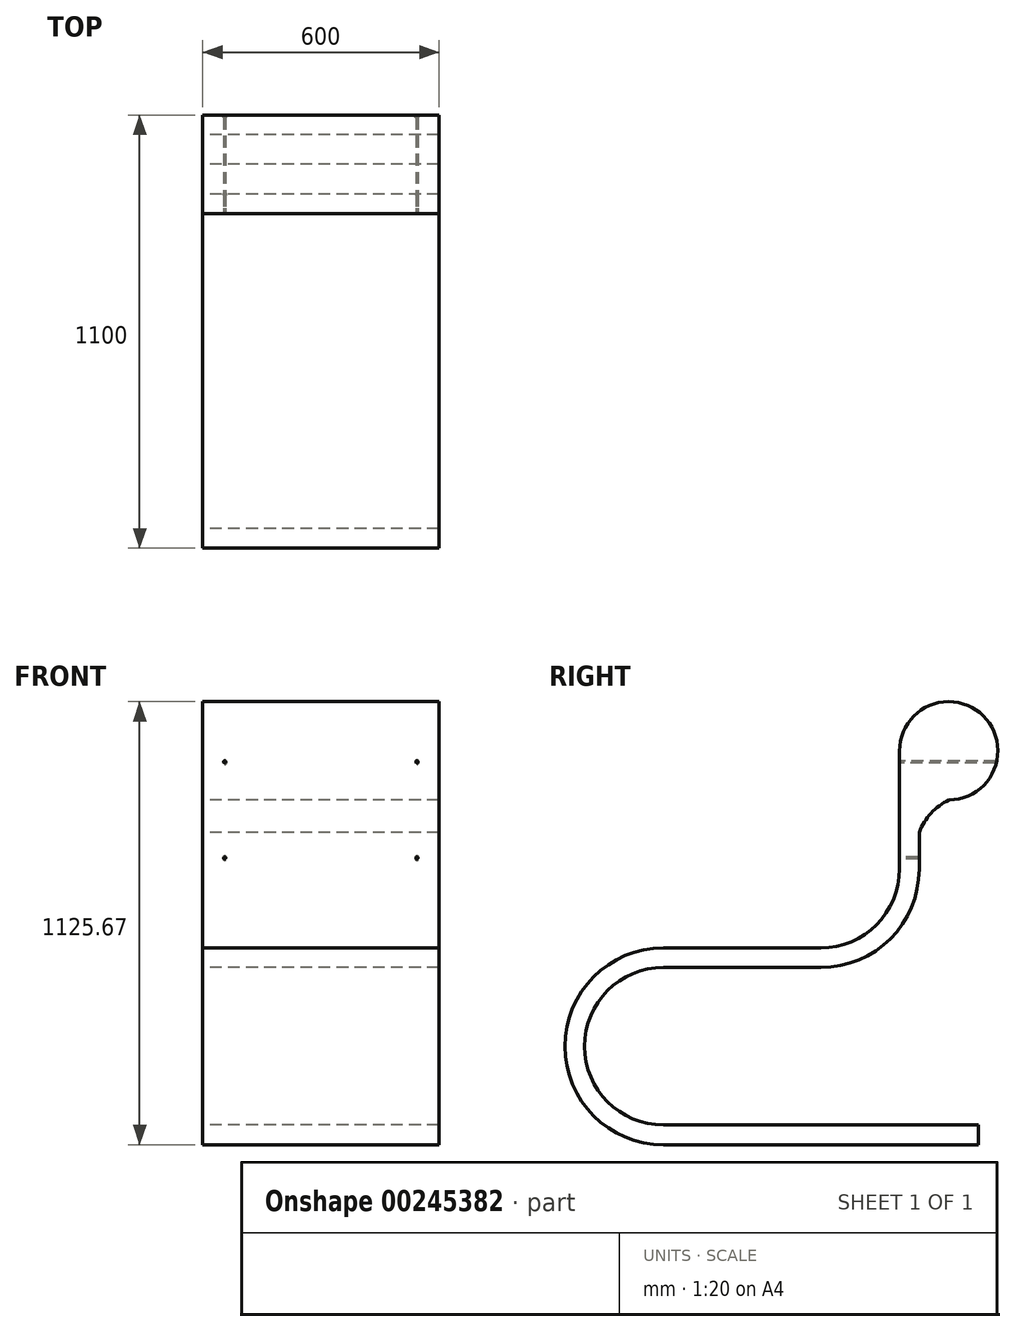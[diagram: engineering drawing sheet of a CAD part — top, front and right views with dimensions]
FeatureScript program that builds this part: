
annotation { "Feature Type Name" : "Feature", "Feature Type Description" : "" }
export const myFeature = defineFeature(function(context is Context, id is Id, definition is map)
    precondition{}
    {
        {
            var Q0;
            Q0=qCreatedBy(makeId("Right.planeOp"),FACE);
            var sketch = newSketch(context, id + "F0", { "sketchPlane" : qUnion([Q0])});
            skLineSegment(sketch, "E0", {"start": v(0, 0) * mm, "end": v(200, 0) * mm});
            skLineSegment(sketch, "E1", {"start": v(0, 0) * mm, "end": v(-200, 0) * mm});
            skLineSegment(sketch, "E2", {"start": v(200, 0) * mm, "end": v(200, 200) * mm});
            skArc(sketch, "E3", {"start": v(200, 0) * mm, "mid": v(341.42, 58.58) * mm, "end": v(400, 200) * mm});
            skLineSegment(sketch, "E4", {"start": v(-200, 0) * mm, "end": v(-200, -500) * mm});
            skArc(sketch, "E5", {"start": v(-200, 0) * mm, "mid": v(-450, -250) * mm, "end": v(-200, -500) * mm});
            skPoint(sketch, "E6", {"position": v(-200, -50) * mm});
            skPoint(sketch, "E7", {"position": v(-200, -450) * mm});
            skArc(sketch, "E8", {"start": v(-200, -50) * mm, "mid": v(-400, -250) * mm, "end": v(-200, -450) * mm});
            skLineSegment(sketch, "E9", {"start": v(-200, -50) * mm, "end": v(200, -50) * mm});
            skArc(sketch, "E10", {"start": v(200, -50) * mm, "mid": v(376.78, 23.22) * mm, "end": v(450, 200) * mm});
            skLineSegment(sketch, "E11.bottom", {"start": v(-200, -450) * mm, "end": v(600, -450) * mm});
            skLineSegment(sketch, "E11.top", {"start": v(-200, -500) * mm, "end": v(600, -500) * mm});
            skLineSegment(sketch, "E11.left", {"start": v(-200, -450) * mm, "end": v(-200, -500) * mm});
            skLineSegment(sketch, "E11.right", {"start": v(600, -450) * mm, "end": v(600, -500) * mm});
            skLineSegment(sketch, "E12.bottom", {"start": v(400, 200) * mm, "end": v(450, 200) * mm});
            skLineSegment(sketch, "E12.top", {"start": v(400, 500.67) * mm, "end": v(450, 500.67) * mm});
            skLineSegment(sketch, "E12.left", {"start": v(400, 200) * mm, "end": v(400, 500.67) * mm});
            skLineSegment(sketch, "E12.right", {"start": v(450, 200) * mm, "end": v(450, 500.67) * mm});
            skArc(sketch, "E13", {"start": v(400, 500.67) * mm, "mid": v(636.8, 556.57) * mm, "end": v(450, 400.67) * mm});
            skArc(sketch, "E14", {"start": v(526.03, 375.68) * mm, "mid": v(480.12, 342.1) * mm, "end": v(450, 293.85) * mm});
            skSolve(sketch);
        }
        {
            var Q0;
            {var subQ0=sQuery(id+"F0.wireOp",EDGE,"E12.top");Q0=makeQuery(id+"F0.imprint","IMPRINT",FACE,{"disambiguationData":[TD([[makeQuery(id+"F0.imprint","IMPRINT",EDGE,{"derivedFrom":subQ0}),1.0]])]});}
            var Q1;
            {var subQ3=sQuery(id+"F0.wireOp",EDGE,"E14");Q1=makeQuery(id+"F0.imprint","IMPRINT",FACE,{"disambiguationData":[TD([[makeQuery(id+"F0.imprint","IMPRINT",EDGE,{"derivedFrom":subQ3}),-1.0]])]});}
            var Q2;
            {var subQ1=sQuery(id+"F0.wireOp",EDGE,"E12.bottom");Q2=makeQuery(id+"F0.imprint","IMPRINT",FACE,{"disambiguationData":[TD([[makeQuery(id+"F0.imprint","IMPRINT",EDGE,{"derivedFrom":subQ1}),1.0]])]});}
            var Q3;
            Q3=makeQuery(id+"F0.imprint","IMPRINT",FACE,{"disambiguationData":[TD([[makeQuery(id+"F0.imprint","IMPRINT",EDGE,{"derivedFrom":sQuery(id+"F0.wireOp",EDGE,"E0")}),-1.0]])]});
            var Q4;
            {var subQ0=sQuery(id+"F0.wireOp",EDGE,"E5");Q4=makeQuery(id+"F0.imprint","IMPRINT",FACE,{"disambiguationData":[TD([[makeQuery(id+"F0.imprint","IMPRINT",EDGE,{"derivedFrom":subQ0}),1.0]])]});}
            var Q5;
            Q5=makeQuery(id+"F0.imprint","IMPRINT",FACE,{"disambiguationData":[TD([[makeQuery(id+"F0.imprint","IMPRINT",EDGE,{"derivedFrom":sQuery(id+"F0.wireOp",EDGE,"E11.bottom")}),-1.0]])]});
            extrude(context, id + "F1", {"entities" : qUnion([Q0, Q1, Q2, Q3, Q4, Q5]), "depth" : 600 * mm});
        }
        {
            var Q0;
            Q0=makeQuery(id+"F1.opExtrude","SWEPT_FACE",FACE,{"disambiguationData":[OSD([sQuery(id+"F0.wireOp",EDGE,"E12.left")])]});
            var sketch = newSketch(context, id + "F2", { "sketchPlane" : qUnion([Q0])});
            skLineSegment(sketch, "E15", {"start": v(0, 500.67) * mm, "end": v(600, 200) * mm});
            skLineSegment(sketch, "E16", {"start": v(600, 500.67) * mm, "end": v(0, 200) * mm});
            skLineSegment(sketch, "E17", {"start": v(55.87, 472.67) * mm, "end": v(55.87, 228) * mm});
            skLineSegment(sketch, "E18", {"start": v(55.87, 228) * mm, "end": v(544.13, 228) * mm});
            skLineSegment(sketch, "E19", {"start": v(544.13, 228) * mm, "end": v(544.13, 472.67) * mm});
            skLineSegment(sketch, "E20", {"start": v(544.13, 472.67) * mm, "end": v(55.87, 472.67) * mm});
            skCircle(sketch, "E21", {"center": v(55.87, 228) * mm, "radius": 2.5 * mm});
            skCircle(sketch, "E22", {"center": v(55.87, 472.67) * mm, "radius": 2.5 * mm});
            skCircle(sketch, "E23", {"center": v(544.13, 472.67) * mm, "radius": 2.5 * mm});
            skCircle(sketch, "E24", {"center": v(544.13, 228) * mm, "radius": 2.5 * mm});
            skSolve(sketch);
        }
        {
            var Q0;
            {var subQ1=sQuery(id+"F2.wireOp",EDGE,"E15");var subQ3=sQuery(id+"F2.wireOp",EDGE,"E22");var subQ4=makeQuery(id+"F2.imprint","INTERSECT",VERTEX,{"disambiguationData":[OD(0.0)],"derivedFrom":[subQ1,subQ3]});Q0=makeQuery(id+"F2.imprint","IMPRINT",FACE,{"disambiguationData":[TD([[makeQuery(id+"F2.imprint","IMPRINT",EDGE,{"disambiguationData":[TD([[subQ4,-1.0]])],"derivedFrom":subQ3}),1.0]])]});}
            var Q1;
            {var subQ1=sQuery(id+"F2.wireOp",EDGE,"E15");var subQ3=sQuery(id+"F2.wireOp",EDGE,"E22");var subQ4=makeQuery(id+"F2.imprint","INTERSECT",VERTEX,{"disambiguationData":[OD(0.0)],"derivedFrom":[subQ1,subQ3]});Q1=makeQuery(id+"F2.imprint","IMPRINT",FACE,{"disambiguationData":[TD([[makeQuery(id+"F2.imprint","IMPRINT",EDGE,{"disambiguationData":[TD([[subQ4,1.0]])],"derivedFrom":subQ3}),1.0]])]});}
            var Q2;
            {var subQ1=sQuery(id+"F2.wireOp",EDGE,"E15");var subQ3=sQuery(id+"F2.wireOp",EDGE,"E22");var subQ4=makeQuery(id+"F2.imprint","INTERSECT",VERTEX,{"disambiguationData":[OD(1.0)],"derivedFrom":[subQ1,subQ3]});Q2=makeQuery(id+"F2.imprint","IMPRINT",FACE,{"disambiguationData":[TD([[makeQuery(id+"F2.imprint","IMPRINT",EDGE,{"disambiguationData":[TD([[subQ4,1.0]])],"derivedFrom":subQ3}),1.0]])]});}
            var Q3;
            {var subQ1=sQuery(id+"F2.wireOp",EDGE,"E15");var subQ3=sQuery(id+"F2.wireOp",EDGE,"E22");var subQ4=makeQuery(id+"F2.imprint","INTERSECT",VERTEX,{"disambiguationData":[OD(1.0)],"derivedFrom":[subQ1,subQ3]});Q3=makeQuery(id+"F2.imprint","IMPRINT",FACE,{"disambiguationData":[TD([[makeQuery(id+"F2.imprint","IMPRINT",EDGE,{"disambiguationData":[TD([[subQ4,-1.0]])],"derivedFrom":subQ3}),1.0]])]});}
            var Q4;
            {var subQ1=sQuery(id+"F2.wireOp",EDGE,"E16");var subQ3=sQuery(id+"F2.wireOp",EDGE,"E21");var subQ4=makeQuery(id+"F2.imprint","INTERSECT",VERTEX,{"disambiguationData":[OD(0.0)],"derivedFrom":[subQ1,subQ3]});Q4=makeQuery(id+"F2.imprint","IMPRINT",FACE,{"disambiguationData":[TD([[makeQuery(id+"F2.imprint","IMPRINT",EDGE,{"disambiguationData":[TD([[subQ4,1.0]])],"derivedFrom":subQ3}),1.0]])]});}
            var Q5;
            {var subQ1=sQuery(id+"F2.wireOp",EDGE,"E16");var subQ3=sQuery(id+"F2.wireOp",EDGE,"E21");var subQ4=makeQuery(id+"F2.imprint","INTERSECT",VERTEX,{"disambiguationData":[OD(0.0)],"derivedFrom":[subQ1,subQ3]});Q5=makeQuery(id+"F2.imprint","IMPRINT",FACE,{"disambiguationData":[TD([[makeQuery(id+"F2.imprint","IMPRINT",EDGE,{"disambiguationData":[TD([[subQ4,-1.0]])],"derivedFrom":subQ3}),1.0]])]});}
            var Q6;
            {var subQ1=sQuery(id+"F2.wireOp",EDGE,"E16");var subQ3=sQuery(id+"F2.wireOp",EDGE,"E21");var subQ4=makeQuery(id+"F2.imprint","INTERSECT",VERTEX,{"disambiguationData":[OD(1.0)],"derivedFrom":[subQ1,subQ3]});Q6=makeQuery(id+"F2.imprint","IMPRINT",FACE,{"disambiguationData":[TD([[makeQuery(id+"F2.imprint","IMPRINT",EDGE,{"disambiguationData":[TD([[subQ4,1.0]])],"derivedFrom":subQ3}),1.0]])]});}
            var Q7;
            {var subQ1=sQuery(id+"F2.wireOp",EDGE,"E16");var subQ3=sQuery(id+"F2.wireOp",EDGE,"E21");var subQ4=makeQuery(id+"F2.imprint","INTERSECT",VERTEX,{"disambiguationData":[OD(1.0)],"derivedFrom":[subQ1,subQ3]});Q7=makeQuery(id+"F2.imprint","IMPRINT",FACE,{"disambiguationData":[TD([[makeQuery(id+"F2.imprint","IMPRINT",EDGE,{"disambiguationData":[TD([[subQ4,-1.0]])],"derivedFrom":subQ3}),1.0]])]});}
            var Q8;
            {var subQ1=sQuery(id+"F2.wireOp",EDGE,"E15");var subQ3=sQuery(id+"F2.wireOp",EDGE,"E24");var subQ4=makeQuery(id+"F2.imprint","INTERSECT",VERTEX,{"disambiguationData":[OD(0.0)],"derivedFrom":[subQ1,subQ3]});Q8=makeQuery(id+"F2.imprint","IMPRINT",FACE,{"disambiguationData":[TD([[makeQuery(id+"F2.imprint","IMPRINT",EDGE,{"disambiguationData":[TD([[subQ4,1.0]])],"derivedFrom":subQ3}),1.0]])]});}
            var Q9;
            {var subQ1=sQuery(id+"F2.wireOp",EDGE,"E15");var subQ3=sQuery(id+"F2.wireOp",EDGE,"E24");var subQ4=makeQuery(id+"F2.imprint","INTERSECT",VERTEX,{"disambiguationData":[OD(1.0)],"derivedFrom":[subQ1,subQ3]});Q9=makeQuery(id+"F2.imprint","IMPRINT",FACE,{"disambiguationData":[TD([[makeQuery(id+"F2.imprint","IMPRINT",EDGE,{"disambiguationData":[TD([[subQ4,-1.0]])],"derivedFrom":subQ3}),1.0]])]});}
            var Q10;
            {var subQ1=sQuery(id+"F2.wireOp",EDGE,"E15");var subQ3=sQuery(id+"F2.wireOp",EDGE,"E24");var subQ4=makeQuery(id+"F2.imprint","INTERSECT",VERTEX,{"disambiguationData":[OD(1.0)],"derivedFrom":[subQ1,subQ3]});Q10=makeQuery(id+"F2.imprint","IMPRINT",FACE,{"disambiguationData":[TD([[makeQuery(id+"F2.imprint","IMPRINT",EDGE,{"disambiguationData":[TD([[subQ4,1.0]])],"derivedFrom":subQ3}),1.0]])]});}
            var Q11;
            {var subQ1=sQuery(id+"F2.wireOp",EDGE,"E15");var subQ3=sQuery(id+"F2.wireOp",EDGE,"E24");var subQ4=makeQuery(id+"F2.imprint","INTERSECT",VERTEX,{"disambiguationData":[OD(0.0)],"derivedFrom":[subQ1,subQ3]});Q11=makeQuery(id+"F2.imprint","IMPRINT",FACE,{"disambiguationData":[TD([[makeQuery(id+"F2.imprint","IMPRINT",EDGE,{"disambiguationData":[TD([[subQ4,-1.0]])],"derivedFrom":subQ3}),1.0]])]});}
            var Q12;
            {var subQ1=sQuery(id+"F2.wireOp",EDGE,"E16");var subQ3=sQuery(id+"F2.wireOp",EDGE,"E23");var subQ4=makeQuery(id+"F2.imprint","INTERSECT",VERTEX,{"disambiguationData":[OD(0.0)],"derivedFrom":[subQ1,subQ3]});Q12=makeQuery(id+"F2.imprint","IMPRINT",FACE,{"disambiguationData":[TD([[makeQuery(id+"F2.imprint","IMPRINT",EDGE,{"disambiguationData":[TD([[subQ4,-1.0]])],"derivedFrom":subQ3}),1.0]])]});}
            var Q13;
            {var subQ1=sQuery(id+"F2.wireOp",EDGE,"E16");var subQ3=sQuery(id+"F2.wireOp",EDGE,"E23");var subQ4=makeQuery(id+"F2.imprint","INTERSECT",VERTEX,{"disambiguationData":[OD(0.0)],"derivedFrom":[subQ1,subQ3]});Q13=makeQuery(id+"F2.imprint","IMPRINT",FACE,{"disambiguationData":[TD([[makeQuery(id+"F2.imprint","IMPRINT",EDGE,{"disambiguationData":[TD([[subQ4,1.0]])],"derivedFrom":subQ3}),1.0]])]});}
            var Q14;
            {var subQ1=sQuery(id+"F2.wireOp",EDGE,"E16");var subQ3=sQuery(id+"F2.wireOp",EDGE,"E23");var subQ4=makeQuery(id+"F2.imprint","INTERSECT",VERTEX,{"disambiguationData":[OD(1.0)],"derivedFrom":[subQ1,subQ3]});Q14=makeQuery(id+"F2.imprint","IMPRINT",FACE,{"disambiguationData":[TD([[makeQuery(id+"F2.imprint","IMPRINT",EDGE,{"disambiguationData":[TD([[subQ4,-1.0]])],"derivedFrom":subQ3}),1.0]])]});}
            var Q15;
            {var subQ1=sQuery(id+"F2.wireOp",EDGE,"E16");var subQ3=sQuery(id+"F2.wireOp",EDGE,"E23");var subQ4=makeQuery(id+"F2.imprint","INTERSECT",VERTEX,{"disambiguationData":[OD(1.0)],"derivedFrom":[subQ1,subQ3]});Q15=makeQuery(id+"F2.imprint","IMPRINT",FACE,{"disambiguationData":[TD([[makeQuery(id+"F2.imprint","IMPRINT",EDGE,{"disambiguationData":[TD([[subQ4,1.0]])],"derivedFrom":subQ3}),1.0]])]});}
            extrude(context, id + "F3", {"entities" : qUnion([Q0, Q1, Q2, Q3, Q4, Q5, Q6, Q7, Q8, Q9, Q10, Q11, Q12, Q13, Q14, Q15]), "operationType" : NewBodyOperationType.REMOVE, "oppositeDirection" : true, "depth" : 300 * mm});
        }
        {
            var Q0;
            Q0=makeQuery(id+"F3.boolean.opBoolean","INTERSECT",EDGE,{"derivedFrom":[makeQuery(id+"F1.opExtrude","SWEPT_FACE",FACE,{"disambiguationData":[OSD([sQuery(id+"F0.wireOp",EDGE,"E13")])]}),makeQuery(id+"F3.opExtrude","SWEPT_FACE",FACE,{"disambiguationData":[OSD([sQuery(id+"F2.wireOp",EDGE,"E23")])]})]});
            chamfer(context, id + "F4", {"entities" : qUnion([Q0]), "width" : 3 * mm, "tangentPropagation" : true});
        }
        {
            var Q0;
            Q0=makeQuery(id+"F3.boolean.opBoolean","INTERSECT",EDGE,{"derivedFrom":[makeQuery(id+"F1.opExtrude","SWEPT_FACE",FACE,{"disambiguationData":[OSD([sQuery(id+"F0.wireOp",EDGE,"E13")])]}),makeQuery(id+"F3.opExtrude","SWEPT_FACE",FACE,{"disambiguationData":[OSD([sQuery(id+"F2.wireOp",EDGE,"E22")])]})]});
            var Q1;
            Q1=makeQuery(id+"F3.boolean.opBoolean","INTERSECT",EDGE,{"derivedFrom":[makeQuery(id+"F1.opExtrude","SWEPT_FACE",FACE,{"disambiguationData":[OSD([sQuery(id+"F0.wireOp",EDGE,"E12.right")])]}),makeQuery(id+"F3.opExtrude","SWEPT_FACE",FACE,{"disambiguationData":[OSD([sQuery(id+"F2.wireOp",EDGE,"E24")])]})]});
            var Q2;
            Q2=makeQuery(id+"F3.boolean.opBoolean","INTERSECT",EDGE,{"derivedFrom":[makeQuery(id+"F1.opExtrude","SWEPT_FACE",FACE,{"disambiguationData":[OSD([sQuery(id+"F0.wireOp",EDGE,"E12.right")])]}),makeQuery(id+"F3.opExtrude","SWEPT_FACE",FACE,{"disambiguationData":[OSD([sQuery(id+"F2.wireOp",EDGE,"E21")])]})]});
            chamfer(context, id + "F5", {"entities" : qUnion([Q0, Q1, Q2]), "width" : 3 * mm, "tangentPropagation" : true});
        }
    });
